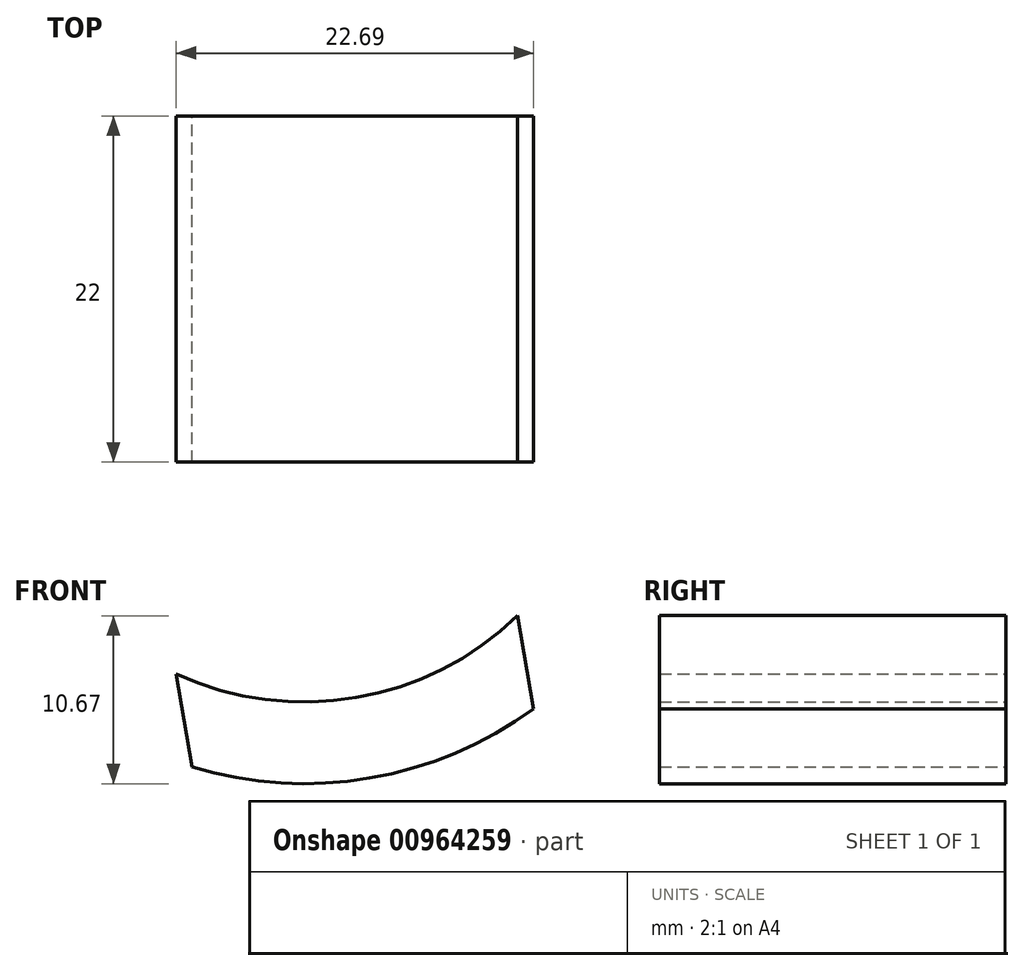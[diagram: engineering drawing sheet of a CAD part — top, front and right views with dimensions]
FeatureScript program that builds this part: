
annotation { "Feature Type Name" : "Feature", "Feature Type Description" : "" }
export const myFeature = defineFeature(function(context is Context, id is Id, definition is map)
    precondition{}
    {
        {
            var Q0;
            Q0=qCreatedBy(makeId("Front.planeOp"),FACE);
            var sketch = newSketch(context, id + "F0", { "sketchPlane" : qUnion([Q0])});
            skLineSegment(sketch, "E0", {"start": v(-39.9, 1.86) * mm, "end": v(-40.41, 4.82) * mm});
            skLineSegment(sketch, "E1", {"start": v(-18.22, 5.57) * mm, "end": v(-18.73, 8.52) * mm});
            skLineSegment(sketch, "E2", {"start": v(-18.22, 5.57) * mm, "end": v(-17.72, 2.6) * mm});
            skLineSegment(sketch, "E3", {"start": v(-39.9, 1.86) * mm, "end": v(-39.4, -1.1) * mm});
            skCircle(sketch, "E4", {"center": v(-32.28, 22.5) * mm, "radius": 19.46 * mm});
            skCircle(sketch, "E5", {"center": v(-32.28, 22.5) * mm, "radius": 24.64 * mm});
            skSolve(sketch);
        }
        {
            var Q0;
            {var subQ3=sQuery(id+"F0.wireOp",EDGE,"E0");Q0=makeQuery(id+"F0.imprint","IMPRINT",FACE,{"disambiguationData":[TD([[makeQuery(id+"F0.imprint","IMPRINT",EDGE,{"derivedFrom":subQ3}),-1.0]])]});}
            extrude(context, id + "F1", {"entities" : qUnion([Q0]), "depth" : 22 * mm, "offsetDistance" : 25 * mm});
        }
    });
